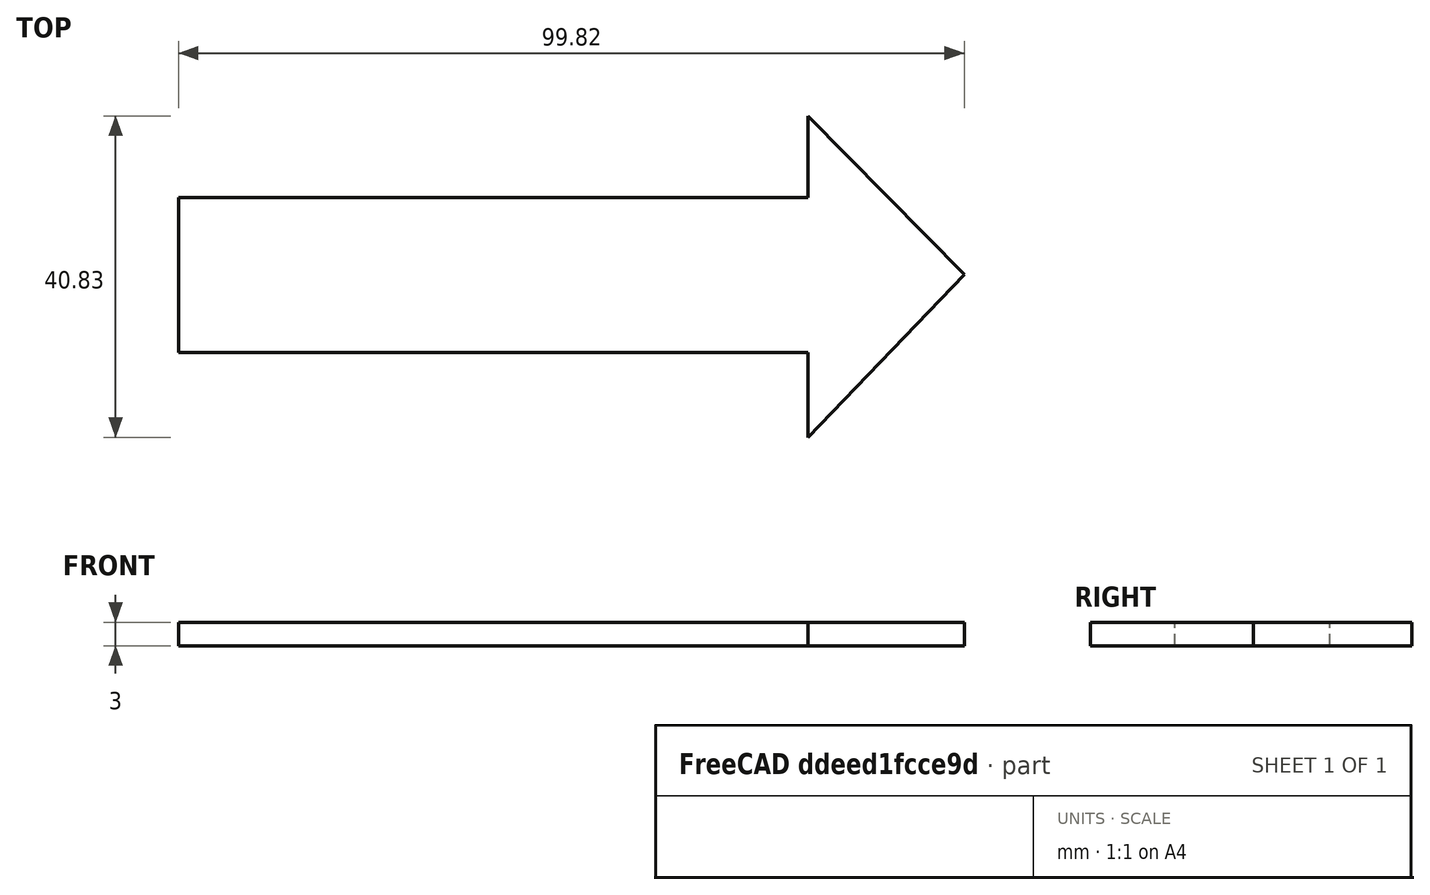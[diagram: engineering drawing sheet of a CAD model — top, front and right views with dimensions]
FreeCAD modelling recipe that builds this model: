
FCSTD DOCUMENT  (FreeCAD 0.21R33694 (Git))
Label: OJT1_T016_Fletxa
License: All rights reserved
LicenseURL: https://en.wikipedia.org/wiki/All_rights_reserved
objects: Sketcher::SketchObject×1, PartDesign::Pad×1, PartDesign::Body×1
note: 4 computed .brp shape members not serialized (recipe doc carries the construction recipe); baked Part::Feature solids carry a one-line shape summary decoded from their .brp

FEATURE [Sketcher::SketchObject] Sketch
  FullyConstrained = false
  MapMode = 5
  Support = -> [XY_Plane]
  sketch-geometry (7):
    g0: LineSegment StartX=-40.0756 StartY=9.73535 StartZ=0 EndX=39.8866 EndY=9.73535 EndZ=0
    g1: LineSegment StartX=39.8866 StartY=9.73535 StartZ=0 EndX=39.8866 EndY=20.1323 EndZ=0
    g2: LineSegment StartX=39.8866 StartY=20.1323 StartZ=0 EndX=59.7354 EndY=0 EndZ=0
    g3: LineSegment StartX=59.7354 StartY=0 StartZ=0 EndX=39.8866 EndY=-20.6994 EndZ=0
    g4: LineSegment StartX=39.8866 StartY=-20.6994 StartZ=0 EndX=39.8866 EndY=-9.92438 EndZ=0
    g5: LineSegment StartX=39.8866 StartY=-9.92438 StartZ=0 EndX=-40.0756 EndY=-9.92438 EndZ=0
    g6: LineSegment StartX=-40.0756 StartY=-9.92438 StartZ=0 EndX=-40.0756 EndY=9.73535 EndZ=0
  constraints (12):
    c: Horizontal(g0)
    c: Coincident(g1,g0)
    c: Vertical(g1)
    c: Coincident(g2,g1)
    c: PointOnObject(g2,g-1)
    c: Coincident(g3,g2)
    c: Coincident(g4,g3)
    c: Vertical(g4)
    c: Horizontal(g5)
    c: Coincident(g6,g5)
    c: Coincident(g6,g0)
    c: Vertical(g6)
FEATURE [PartDesign::Pad] Pad
  Direction = (0,0,1)
  Length = 3
  Length2 = 10
  Profile = -> Sketch
  ReferenceAxis = -> Sketch [N_Axis]
  Type = 0
FEATURE [PartDesign::Body] Body
  Group = -> [Sketch,Pad]
  Origin = -> Origin
  Tip = -> Pad
